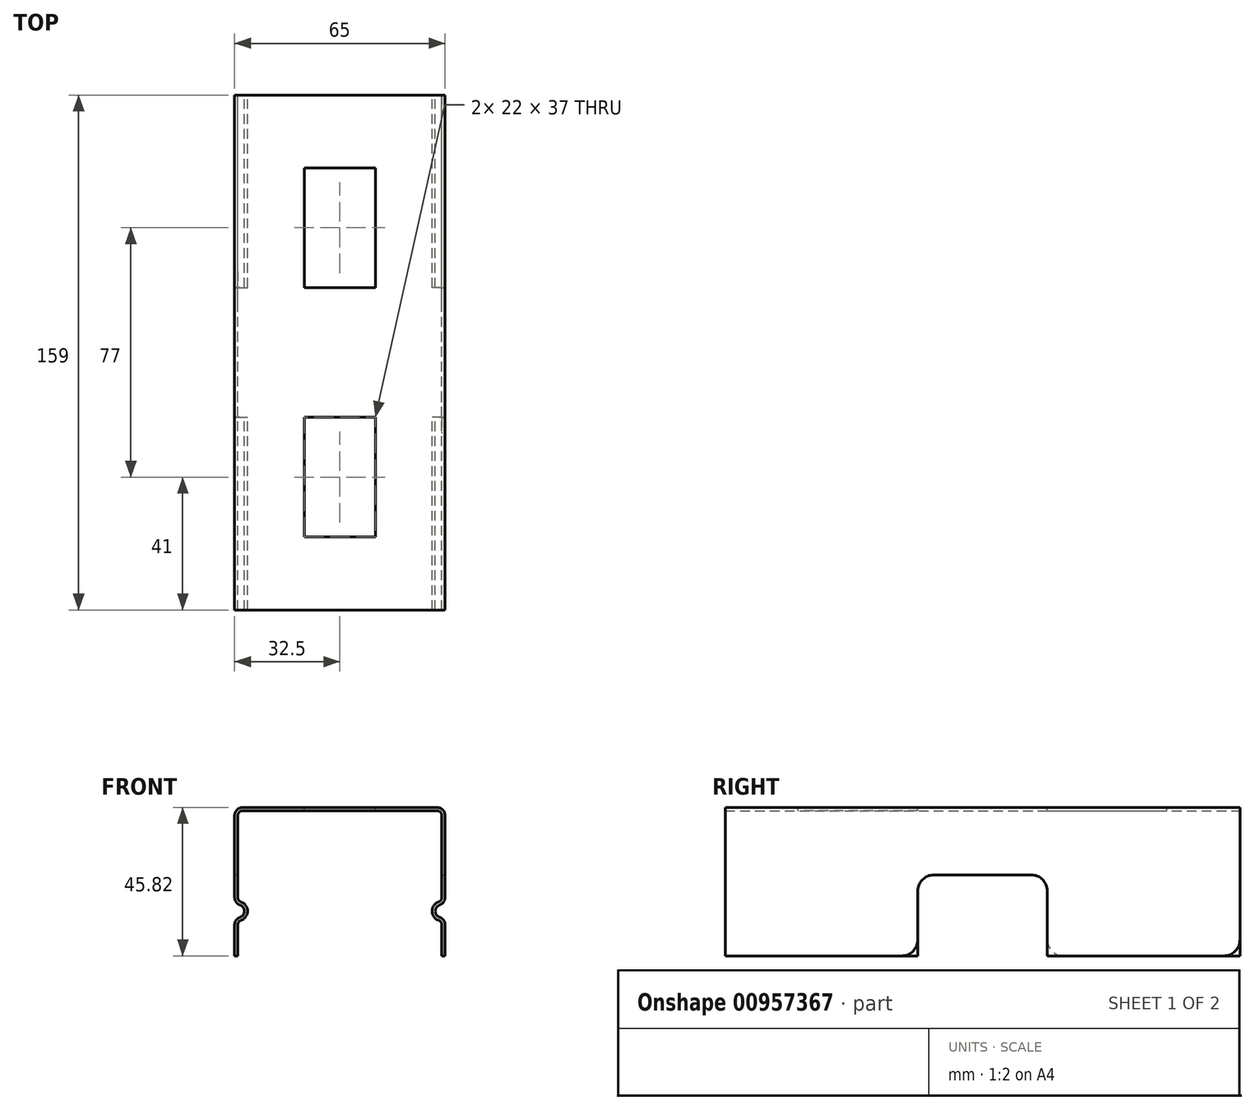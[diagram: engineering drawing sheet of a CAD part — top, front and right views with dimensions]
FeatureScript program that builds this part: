
annotation { "Feature Type Name" : "Feature", "Feature Type Description" : "" }
export const myFeature = defineFeature(function(context is Context, id is Id, definition is map)
    precondition{}
    {
        {
            var Q0;
            Q0=qCreatedBy(makeId("Front.planeOp"),FACE);
            var sketch = newSketch(context, id + "F0", { "sketchPlane" : qUnion([Q0])});
            skArc(sketch, "E0", {"start": v(0.67, -1.89) * mm, "mid": v(2, 0) * mm, "end": v(0.67, 1.89) * mm});
            skArc(sketch, "E1", {"start": v(1, -2.83) * mm, "mid": v(3, 0) * mm, "end": v(1, 2.83) * mm});
            skLineSegment(sketch, "E2", {"start": v(0, -13.82) * mm, "end": v(0, -4.24) * mm});
            skLineSegment(sketch, "E3.0", {"start": v(-1, 4.24) * mm, "end": v(-1, 29.5) * mm});
            skLineSegment(sketch, "E4", {"start": v(-1, -4.24) * mm, "end": v(-1, -13.82) * mm});
            skLineSegment(sketch, "E5.trimOffspring", {"start": v(0, -2) * mm, "end": v(0, 2) * mm});
            skLineSegment(sketch, "E6.trimOffspring", {"start": v(0, 4.24) * mm, "end": v(0, 29.5) * mm});
            skPoint(sketch, "E7.visualSharp", {"position": v(0, 3) * mm});
            skArc(sketch, "E7.filletArc", {"start": v(0, 4.24) * mm, "mid": v(0.28, 3.38) * mm, "end": v(1, 2.83) * mm});
            skPoint(sketch, "E8.visualSharp", {"position": v(0, -3) * mm});
            skArc(sketch, "E8.filletArc", {"start": v(1, -2.83) * mm, "mid": v(0.28, -3.38) * mm, "end": v(0, -4.24) * mm});
            skArc(sketch, "E9.filletArc", {"start": v(0.67, -1.89) * mm, "mid": v(-0.54, -2.8) * mm, "end": v(-1, -4.24) * mm});
            skArc(sketch, "E10.filletArc", {"start": v(-1, 4.24) * mm, "mid": v(-0.54, 2.8) * mm, "end": v(0.67, 1.89) * mm});
            skLineSegment(sketch, "E11", {"start": v(-1, -13.82) * mm, "end": v(0, -13.82) * mm});
            skLineSegment(sketch, "E12", {"start": v(1.5, 32) * mm, "end": v(61.5, 32) * mm});
            skLineSegment(sketch, "E13", {"start": v(31.5, 37.3) * mm, "end": v(31.5, -8.9) * mm, "construction": true});
            skArc(sketch, "E14.MirrorCS", {"start": v(63, 4.24) * mm, "mid": v(62.72, 3.38) * mm, "end": v(62, 2.83) * mm});
            skArc(sketch, "E15.MirrorCS", {"start": v(62, -2.83) * mm, "mid": v(62.72, -3.38) * mm, "end": v(63, -4.24) * mm});
            skArc(sketch, "E16.MirrorCS", {"start": v(62.33, -1.89) * mm, "mid": v(63.54, -2.8) * mm, "end": v(64, -4.24) * mm});
            skLineSegment(sketch, "E17.MirrorCS", {"start": v(64, -13.82) * mm, "end": v(63, -13.82) * mm});
            skArc(sketch, "E18.MirrorCS", {"start": v(64, 4.24) * mm, "mid": v(63.54, 2.8) * mm, "end": v(62.33, 1.89) * mm});
            skLineSegment(sketch, "E19.MirrorCS", {"start": v(63, -2) * mm, "end": v(63, 2) * mm});
            skArc(sketch, "E20.MirrorCS", {"start": v(62, -2.83) * mm, "mid": v(60, 0) * mm, "end": v(62, 2.83) * mm});
            skLineSegment(sketch, "E21.MirrorCS", {"start": v(64, 4.24) * mm, "end": v(64, 29.5) * mm});
            skLineSegment(sketch, "E22.MirrorCS", {"start": v(64, -4.24) * mm, "end": v(64, -13.82) * mm});
            skPoint(sketch, "E23.MirrorP", {"position": v(63, -3) * mm});
            skLineSegment(sketch, "E24.MirrorCS", {"start": v(63, -13.82) * mm, "end": v(63, -4.24) * mm});
            skLineSegment(sketch, "E25.MirrorCS", {"start": v(63, 4.24) * mm, "end": v(63, 29.5) * mm});
            skArc(sketch, "E26.MirrorCS", {"start": v(62.33, -1.89) * mm, "mid": v(61, 0) * mm, "end": v(62.33, 1.89) * mm});
            skPoint(sketch, "E27.MirrorP", {"position": v(63, 3) * mm});
            skLineSegment(sketch, "E28.0", {"start": v(1.5, 31) * mm, "end": v(61.5, 31) * mm});
            skPoint(sketch, "E29.newPointB", {"position": v(0, 32) * mm});
            skArc(sketch, "E29.filletArc", {"start": v(1.5, 31) * mm, "mid": v(0.44, 30.56) * mm, "end": v(0, 29.5) * mm});
            skPoint(sketch, "E30.visualSharp", {"position": v(-1, 32) * mm});
            skArc(sketch, "E30.filletArc", {"start": v(1.5, 32) * mm, "mid": v(-0.27, 31.27) * mm, "end": v(-1, 29.5) * mm});
            skPoint(sketch, "E31.visualSharp", {"position": v(64, 32) * mm});
            skArc(sketch, "E31.filletArc", {"start": v(64, 29.5) * mm, "mid": v(63.27, 31.27) * mm, "end": v(61.5, 32) * mm});
            skPoint(sketch, "E32.newPointB", {"position": v(63, 32) * mm});
            skArc(sketch, "E32.filletArc", {"start": v(63, 29.5) * mm, "mid": v(62.56, 30.56) * mm, "end": v(61.5, 31) * mm});
            skSolve(sketch);
        }
        {
            var Q0;
            Q0=makeQuery(id+"F0.imprint","IMPRINT",FACE,{"disambiguationData":[TD([[makeQuery(id+"F0.imprint","IMPRINT",EDGE,{"derivedFrom":sQuery(id+"F0.wireOp",EDGE,"E0")}),-1.0]])]});
            extrude(context, id + "F1", {"entities" : qUnion([Q0]), "depth" : 159 * mm, "offsetDistance" : 25 * mm});
        }
        {
            var Q0;
            Q0=makeQuery(id+"F1.opExtrude","SWEPT_FACE",FACE,{"disambiguationData":[OSD([sQuery(id+"F0.wireOp",EDGE,"E12")])]});
            var sketch = newSketch(context, id + "F2", { "sketchPlane" : qUnion([Q0])});
            skLineSegment(sketch, "E33", {"start": v(31.5, 0) * mm, "end": v(31.5, -159) * mm, "construction": true});
            skLineSegment(sketch, "E34.bottom", {"start": v(42.5, -59.5) * mm, "end": v(20.5, -59.5) * mm});
            skLineSegment(sketch, "E34.top", {"start": v(42.5, -22.5) * mm, "end": v(20.5, -22.5) * mm});
            skLineSegment(sketch, "E34.left", {"start": v(42.5, -59.5) * mm, "end": v(42.5, -22.5) * mm});
            skLineSegment(sketch, "E34.right", {"start": v(20.5, -59.5) * mm, "end": v(20.5, -22.5) * mm});
            skPoint(sketch, "E34.middle", {"position": v(31.5, -41) * mm});
            skLineSegment(sketch, "E35.MirrorCS", {"start": v(20.5, -99.5) * mm, "end": v(20.5, -136.5) * mm});
            skLineSegment(sketch, "E36.MirrorCS", {"start": v(42.5, -99.5) * mm, "end": v(20.5, -99.5) * mm});
            skPoint(sketch, "E37.MirrorP", {"position": v(31.5, -118) * mm});
            skLineSegment(sketch, "E38.MirrorCS", {"start": v(42.5, -136.5) * mm, "end": v(20.5, -136.5) * mm});
            skLineSegment(sketch, "E39.MirrorCS", {"start": v(42.5, -99.5) * mm, "end": v(42.5, -136.5) * mm});
            skSolve(sketch);
        }
        {
            var Q0;
            Q0=makeQuery(id+"F2.imprint","IMPRINT",FACE,{"disambiguationData":[TD([[makeQuery(id+"F2.imprint","IMPRINT",EDGE,{"derivedFrom":sQuery(id+"F2.wireOp",EDGE,"E35.MirrorCS")}),1.0]])]});
            var Q1;
            Q1=makeQuery(id+"F2.imprint","IMPRINT",FACE,{"disambiguationData":[TD([[makeQuery(id+"F2.imprint","IMPRINT",EDGE,{"derivedFrom":sQuery(id+"F2.wireOp",EDGE,"E34.bottom")}),-1.0]])]});
            extrude(context, id + "F3", {"entities" : qUnion([Q0, Q1]), "operationType" : NewBodyOperationType.REMOVE, "endBound" : BoundingType.THROUGH_ALL, "oppositeDirection" : true, "depth" : 25 * mm, "offsetDistance" : 25 * mm});
        }
        {
            var Q0;
            Q0=makeQuery(id+"F1.opExtrude","SWEPT_FACE",FACE,{"disambiguationData":[OSD([sQuery(id+"F0.wireOp",EDGE,"E22.MirrorCS")])]});
            var sketch = newSketch(context, id + "F4", { "sketchPlane" : qUnion([Q0])});
            skLineSegment(sketch, "E40.bottom", {"start": v(-59.5, -13.82) * mm, "end": v(-99.5, -13.82) * mm});
            skLineSegment(sketch, "E40.top", {"start": v(-64.5, 11.18) * mm, "end": v(-94.5, 11.18) * mm});
            skLineSegment(sketch, "E40.left", {"start": v(-59.5, -13.82) * mm, "end": v(-59.5, 6.18) * mm});
            skLineSegment(sketch, "E40.right", {"start": v(-99.5, -13.82) * mm, "end": v(-99.5, 6.18) * mm});
            skPoint(sketch, "E40.middle", {"position": v(-79.5, -1.32) * mm});
            skLineSegment(sketch, "E41", {"start": v(-79.5, 63.78) * mm, "end": v(-79.5, -61.46) * mm, "construction": true});
            skPoint(sketch, "E42.visualSharp", {"position": v(-99.5, 11.18) * mm});
            skArc(sketch, "E42.filletArc", {"start": v(-94.5, 11.18) * mm, "mid": v(-98.04, 9.72) * mm, "end": v(-99.5, 6.18) * mm});
            skPoint(sketch, "E43.visualSharp", {"position": v(-59.5, 11.18) * mm});
            skArc(sketch, "E43.filletArc", {"start": v(-59.5, 6.18) * mm, "mid": v(-60.96, 9.72) * mm, "end": v(-64.5, 11.18) * mm});
            skSolve(sketch);
        }
        {
            var Q0;
            Q0=makeQuery(id+"F4.imprint","IMPRINT",FACE,{"disambiguationData":[TD([[makeQuery(id+"F4.imprint","IMPRINT",EDGE,{"derivedFrom":sQuery(id+"F4.wireOp",EDGE,"E40.top")}),1.0]])]});
            var Q1;
            {var subQ0=sQuery(id+"F4.wireOp",EDGE,"E40.bottom");Q1=makeQuery(id+"F4.imprint","IMPRINT",FACE,{"disambiguationData":[TD([[makeQuery(id+"F4.imprint","IMPRINT",EDGE,{"derivedFrom":subQ0}),1.0]])]});}
            extrude(context, id + "F5", {"entities" : qUnion([Q0, Q1]), "operationType" : NewBodyOperationType.REMOVE, "endBound" : BoundingType.THROUGH_ALL, "oppositeDirection" : true, "depth" : 25 * mm, "offsetDistance" : 25 * mm});
        }
        {
            var Q0;
            Q0=makeQuery(id+"F1.opExtrude","CAP_EDGE",EDGE,{"disambiguationData":[OSD([sQuery(id+"F0.wireOp",EDGE,"E17.MirrorCS")])],"isStart":true});
            var Q1;
            {var subQ0=sQuery(id+"F0.wireOp",EDGE,"E17.MirrorCS");var subQ1=sQuery(id+"F4.wireOp",EDGE,"E40.right");Q1=makeQuery(id+"F5.boolean.opBoolean","COPY",EDGE,{"disambiguationData":[topologyDisambiguationEdgeConnected([makeQuery(id+"F1.opExtrude","SWEPT_FACE",FACE,{"disambiguationData":[OSD([subQ0])]})])],"derivedFrom":makeQuery(id+"F5.opExtrude","SWEPT_EDGE",EDGE,{"disambiguationData":[OSD([subQ0,sQuery(id+"F0.wireOp",EDGE,"E22.MirrorCS"),sQuery(id+"F4.wireOp",EDGE,"E40.bottom"),subQ1])]})});}
            var Q2;
            {var subQ0=sQuery(id+"F0.wireOp",EDGE,"E17.MirrorCS");var subQ1=sQuery(id+"F4.wireOp",EDGE,"E40.left");Q2=makeQuery(id+"F5.boolean.opBoolean","COPY",EDGE,{"disambiguationData":[topologyDisambiguationEdgeConnected([makeQuery(id+"F1.opExtrude","SWEPT_FACE",FACE,{"disambiguationData":[OSD([subQ0])]})])],"derivedFrom":makeQuery(id+"F5.opExtrude","SWEPT_EDGE",EDGE,{"disambiguationData":[OSD([subQ0,sQuery(id+"F0.wireOp",EDGE,"E22.MirrorCS"),sQuery(id+"F4.wireOp",EDGE,"E40.bottom"),subQ1])]})});}
            var Q3;
            {var subQ0=sQuery(id+"F4.wireOp",EDGE,"E40.right");Q3=makeQuery(id+"F5.boolean.opBoolean","COPY",EDGE,{"disambiguationData":[topologyDisambiguationEdgeConnected([makeQuery(id+"F1.opExtrude","SWEPT_FACE",FACE,{"disambiguationData":[OSD([sQuery(id+"F0.wireOp",EDGE,"E11")])]})])],"derivedFrom":makeQuery(id+"F5.opExtrude","SWEPT_EDGE",EDGE,{"disambiguationData":[OSD([sQuery(id+"F0.wireOp",EDGE,"E17.MirrorCS"),sQuery(id+"F0.wireOp",EDGE,"E22.MirrorCS"),sQuery(id+"F4.wireOp",EDGE,"E40.bottom"),subQ0])]})});}
            var Q4;
            {var subQ0=sQuery(id+"F4.wireOp",EDGE,"E40.left");Q4=makeQuery(id+"F5.boolean.opBoolean","COPY",EDGE,{"disambiguationData":[topologyDisambiguationEdgeConnected([makeQuery(id+"F1.opExtrude","SWEPT_FACE",FACE,{"disambiguationData":[OSD([sQuery(id+"F0.wireOp",EDGE,"E11")])]})])],"derivedFrom":makeQuery(id+"F5.opExtrude","SWEPT_EDGE",EDGE,{"disambiguationData":[OSD([sQuery(id+"F0.wireOp",EDGE,"E17.MirrorCS"),sQuery(id+"F0.wireOp",EDGE,"E22.MirrorCS"),sQuery(id+"F4.wireOp",EDGE,"E40.bottom"),subQ0])]})});}
            fillet(context, id + "F6", {"entities" : qUnion([Q0, Q1, Q2, Q3, Q4]), "radius" : 5 * mm, "tangentPropagation" : true, "allowEdgeOverflow" : false});
        }
    });
